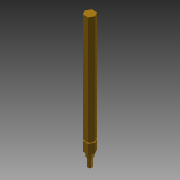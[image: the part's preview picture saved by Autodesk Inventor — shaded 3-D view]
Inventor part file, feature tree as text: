
AUTODESK INVENTOR PART (.ipt)
format: ipt  version: 2014 SP1 (Build 180222100, 222)  size: 106,496 bytes
history: native  units: in
note: dims shown in document units (in); Inventor stores cm internally (conversion verified against a paired STEP export)
features: chamfer x1, other x1, extrude x1, imported_body x1, sketch x1
ambient origin geometry x8: Origin, YZ Plane, XZ Plane, XY Plane, X Axis, Y Axis, Z Axis, Center Point
bodies: Body1 (feature_tree)
feature tree (5):
  chamfer  "Chamfer1"  Distance=3.556in
  other  "TB Output Shaft AM14U1"
  extrude  "Extrusion1"  [1 undecoded]
  imported_body  "Base1"
  sketch  "Sketch1"
note: 1 required parameter value undecoded (feature->parameter linkage not recoverable at this tier; creation-order binding heuristic only, values carry confidence <= 0.55)
